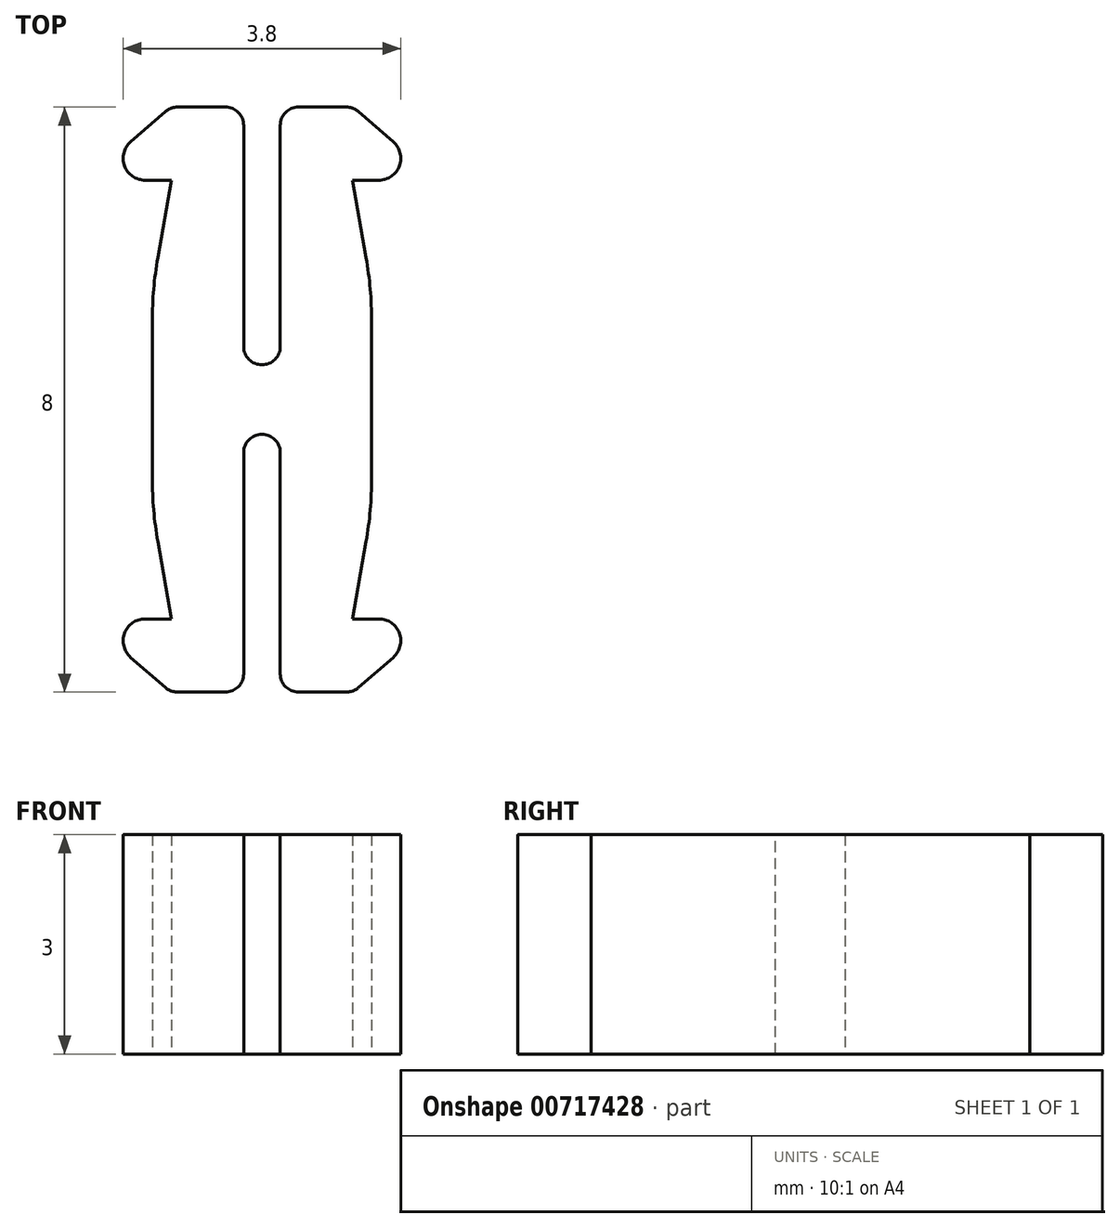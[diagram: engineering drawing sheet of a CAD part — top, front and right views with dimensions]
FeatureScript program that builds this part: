
annotation { "Feature Type Name" : "Feature", "Feature Type Description" : "" }
export const myFeature = defineFeature(function(context is Context, id is Id, definition is map)
    precondition{}
    {
        {
            var Q0;
            Q0=qCreatedBy(makeId("Top.planeOp"),FACE);
            var sketch = newSketch(context, id + "F0", { "sketchPlane" : qUnion([Q0])});
            skLineSegment(sketch, "E0", {"start": v(-1.5, 0) * mm, "end": v(-1.5, 1.51) * mm});
            skLineSegment(sketch, "E1", {"start": v(-1.5, 1.51) * mm, "end": v(-1.24, 3) * mm});
            skLineSegment(sketch, "E2", {"start": v(-1.24, 3) * mm, "end": v(-1.6, 3) * mm});
            skLineSegment(sketch, "E3", {"start": v(-1.8, 3.53) * mm, "end": v(-1.25, 4) * mm});
            skLineSegment(sketch, "E4", {"start": v(-1.25, 4) * mm, "end": v(-0.25, 4) * mm});
            skLineSegment(sketch, "E5", {"start": v(-0.25, 4) * mm, "end": v(-0.25, 0.48) * mm});
            skLineSegment(sketch, "E6", {"start": v(-0.25, 0.48) * mm, "end": v(0, 0.48) * mm});
            skLineSegment(sketch, "E7", {"start": v(0, 0) * mm, "end": v(0, 4) * mm, "construction": true});
            skLineSegment(sketch, "E8", {"start": v(0, 0) * mm, "end": v(-2.4, 0) * mm, "construction": true});
            skLineSegment(sketch, "E9.MirrorCS", {"start": v(1.8, 3.53) * mm, "end": v(1.25, 4) * mm});
            skLineSegment(sketch, "E10.MirrorCS", {"start": v(1.25, 4) * mm, "end": v(0.25, 4) * mm});
            skLineSegment(sketch, "E11.MirrorCS", {"start": v(1.24, 3) * mm, "end": v(1.6, 3) * mm});
            skLineSegment(sketch, "E12.MirrorCS", {"start": v(1.5, 1.51) * mm, "end": v(1.24, 3) * mm});
            skLineSegment(sketch, "E13.MirrorCS", {"start": v(0.25, 4) * mm, "end": v(0.25, 0.48) * mm});
            skLineSegment(sketch, "E14.MirrorCS", {"start": v(0.25, 0.48) * mm, "end": v(0, 0.48) * mm});
            skLineSegment(sketch, "E15.MirrorCS", {"start": v(0.25, -0.48) * mm, "end": v(0, -0.48) * mm});
            skLineSegment(sketch, "E16.MirrorCS", {"start": v(-1.5, -1.51) * mm, "end": v(-1.24, -3) * mm});
            skLineSegment(sketch, "E17.MirrorCS", {"start": v(-1.24, -3) * mm, "end": v(-1.6, -3) * mm});
            skLineSegment(sketch, "E18.MirrorCS", {"start": v(-0.25, -0.48) * mm, "end": v(0, -0.48) * mm});
            skLineSegment(sketch, "E19.MirrorCS", {"start": v(-1.8, -3.53) * mm, "end": v(-1.25, -4) * mm});
            skLineSegment(sketch, "E20.MirrorCS", {"start": v(1.25, -4) * mm, "end": v(0.25, -4) * mm});
            skLineSegment(sketch, "E21.MirrorCS", {"start": v(-1.25, -4) * mm, "end": v(-0.25, -4) * mm});
            skLineSegment(sketch, "E22.MirrorCS", {"start": v(1.24, -3) * mm, "end": v(1.6, -3) * mm});
            skLineSegment(sketch, "E23.MirrorCS", {"start": v(-0.25, -4) * mm, "end": v(-0.25, -0.48) * mm});
            skLineSegment(sketch, "E24.MirrorCS", {"start": v(0.25, -4) * mm, "end": v(0.25, -0.48) * mm});
            skLineSegment(sketch, "E25.MirrorCS", {"start": v(1.5, -1.51) * mm, "end": v(1.24, -3) * mm});
            skLineSegment(sketch, "E26.MirrorCS", {"start": v(1.8, -3.53) * mm, "end": v(1.25, -4) * mm});
            skLineSegment(sketch, "E27.MirrorCS", {"start": v(-1.5, 0) * mm, "end": v(-1.5, -1.51) * mm});
            skLineSegment(sketch, "E28", {"start": v(1.5, -1.51) * mm, "end": v(1.5, 1.51) * mm});
            skPoint(sketch, "E29.visualSharp", {"position": v(-2.4, 3) * mm});
            skArc(sketch, "E29.filletArc", {"start": v(-1.8, 3.53) * mm, "mid": v(-1.88, 3.2) * mm, "end": v(-1.6, 3) * mm});
            skPoint(sketch, "E30.visualSharp", {"position": v(2.4, 3) * mm});
            skArc(sketch, "E30.filletArc", {"start": v(1.6, 3) * mm, "mid": v(1.88, 3.2) * mm, "end": v(1.8, 3.53) * mm});
            skPoint(sketch, "E31.visualSharp", {"position": v(-2.4, -3) * mm});
            skArc(sketch, "E31.filletArc", {"start": v(-1.6, -3) * mm, "mid": v(-1.88, -3.2) * mm, "end": v(-1.8, -3.53) * mm});
            skPoint(sketch, "E32.visualSharp", {"position": v(2.4, -3) * mm});
            skArc(sketch, "E32.filletArc", {"start": v(1.8, -3.53) * mm, "mid": v(1.88, -3.2) * mm, "end": v(1.6, -3) * mm});
            skSolve(sketch);
        }
        {
            var Q0;
            Q0 = qSketchRegion(id + "F0", true);
            extrude(context, id + "F1", {"entities" : qUnion([Q0]), "depth" : 3 * mm, "offsetDistance" : 25 * mm});
        }
        {
            var Q0;
            Q0=makeQuery(id+"F1.opExtrude","SWEPT_EDGE",EDGE,{"disambiguationData":[OSD([sQuery(id+"F0.wireOp",EDGE,"E3"),sQuery(id+"F0.wireOp",EDGE,"E4")])]});
            var Q1;
            Q1=makeQuery(id+"F1.opExtrude","SWEPT_EDGE",EDGE,{"disambiguationData":[OSD([sQuery(id+"F0.wireOp",EDGE,"E4"),sQuery(id+"F0.wireOp",EDGE,"E5")])]});
            var Q2;
            Q2=makeQuery(id+"F1.opExtrude","SWEPT_EDGE",EDGE,{"disambiguationData":[OSD([sQuery(id+"F0.wireOp",EDGE,"E10.MirrorCS"),sQuery(id+"F0.wireOp",EDGE,"E13.MirrorCS")])]});
            var Q3;
            Q3=makeQuery(id+"F1.opExtrude","SWEPT_EDGE",EDGE,{"disambiguationData":[OSD([sQuery(id+"F0.wireOp",EDGE,"E9.MirrorCS"),sQuery(id+"F0.wireOp",EDGE,"E10.MirrorCS")])]});
            var Q4;
            Q4=makeQuery(id+"F1.opExtrude","SWEPT_EDGE",EDGE,{"disambiguationData":[OSD([sQuery(id+"F0.wireOp",EDGE,"E5"),sQuery(id+"F0.wireOp",EDGE,"E6")])]});
            var Q5;
            Q5=makeQuery(id+"F1.opExtrude","SWEPT_EDGE",EDGE,{"disambiguationData":[OSD([sQuery(id+"F0.wireOp",EDGE,"E13.MirrorCS"),sQuery(id+"F0.wireOp",EDGE,"E14.MirrorCS")])]});
            var Q6;
            Q6=makeQuery(id+"F1.opExtrude","SWEPT_EDGE",EDGE,{"disambiguationData":[OSD([sQuery(id+"F0.wireOp",EDGE,"E18.MirrorCS"),sQuery(id+"F0.wireOp",EDGE,"E23.MirrorCS")])]});
            var Q7;
            Q7=makeQuery(id+"F1.opExtrude","SWEPT_EDGE",EDGE,{"disambiguationData":[OSD([sQuery(id+"F0.wireOp",EDGE,"E15.MirrorCS"),sQuery(id+"F0.wireOp",EDGE,"E24.MirrorCS")])]});
            var Q8;
            Q8=makeQuery(id+"F1.opExtrude","SWEPT_EDGE",EDGE,{"disambiguationData":[OSD([sQuery(id+"F0.wireOp",EDGE,"E19.MirrorCS"),sQuery(id+"F0.wireOp",EDGE,"E21.MirrorCS")])]});
            var Q9;
            Q9=makeQuery(id+"F1.opExtrude","SWEPT_EDGE",EDGE,{"disambiguationData":[OSD([sQuery(id+"F0.wireOp",EDGE,"E21.MirrorCS"),sQuery(id+"F0.wireOp",EDGE,"E23.MirrorCS")])]});
            var Q10;
            Q10=makeQuery(id+"F1.opExtrude","SWEPT_EDGE",EDGE,{"disambiguationData":[OSD([sQuery(id+"F0.wireOp",EDGE,"E20.MirrorCS"),sQuery(id+"F0.wireOp",EDGE,"E24.MirrorCS")])]});
            var Q11;
            Q11=makeQuery(id+"F1.opExtrude","SWEPT_EDGE",EDGE,{"disambiguationData":[OSD([sQuery(id+"F0.wireOp",EDGE,"E20.MirrorCS"),sQuery(id+"F0.wireOp",EDGE,"E26.MirrorCS")])]});
            fillet(context, id + "F2", {"entities" : qUnion([Q0, Q1, Q2, Q3, Q4, Q5, Q6, Q7, Q8, Q9, Q10, Q11]), "radius" : 0.25 * mm, "tangentPropagation" : true, "allowEdgeOverflow" : false});
        }
        {
            var Q0;
            Q0=makeQuery(id+"F1.opExtrude","SWEPT_EDGE",EDGE,{"disambiguationData":[OSD([sQuery(id+"F0.wireOp",EDGE,"E16.MirrorCS"),sQuery(id+"F0.wireOp",EDGE,"E27.MirrorCS")])]});
            var Q1;
            Q1=makeQuery(id+"F1.opExtrude","SWEPT_EDGE",EDGE,{"disambiguationData":[OSD([sQuery(id+"F0.wireOp",EDGE,"E0"),sQuery(id+"F0.wireOp",EDGE,"E1")])]});
            var Q2;
            Q2=makeQuery(id+"F1.opExtrude","SWEPT_EDGE",EDGE,{"disambiguationData":[OSD([sQuery(id+"F0.wireOp",EDGE,"E25.MirrorCS"),sQuery(id+"F0.wireOp",EDGE,"E28")])]});
            var Q3;
            Q3=makeQuery(id+"F1.opExtrude","SWEPT_EDGE",EDGE,{"disambiguationData":[OSD([sQuery(id+"F0.wireOp",EDGE,"E12.MirrorCS"),sQuery(id+"F0.wireOp",EDGE,"E28")])]});
            fillet(context, id + "F3", {"entities" : qUnion([Q0, Q1, Q2, Q3]), "radius" : 5 * mm, "tangentPropagation" : true, "allowEdgeOverflow" : false});
        }
    });
